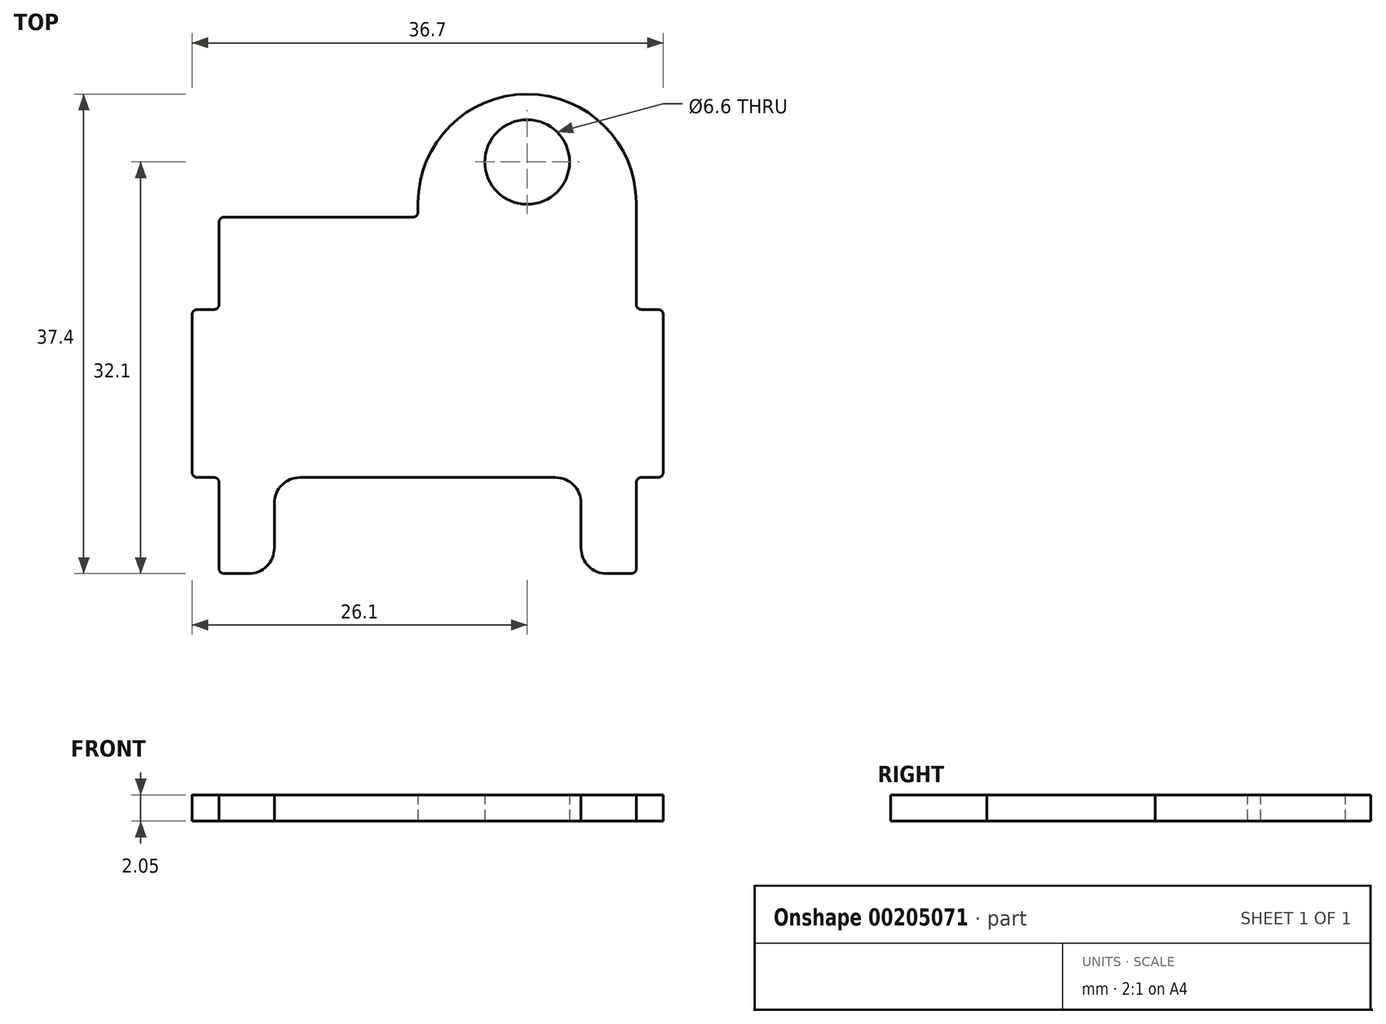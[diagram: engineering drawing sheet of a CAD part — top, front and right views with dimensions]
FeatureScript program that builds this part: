
annotation { "Feature Type Name" : "Feature", "Feature Type Description" : "" }
export const myFeature = defineFeature(function(context is Context, id is Id, definition is map)
    precondition{}
    {
        {
            var Q0;
            Q0=qCreatedBy(makeId("Top.planeOp"),FACE);
            var sketch = newSketch(context, id + "F0", { "sketchPlane" : qUnion([Q0])});
            skLineSegment(sketch, "E0", {"start": v(0, 0) * mm, "end": v(0, -6.8) * mm});
            skLineSegment(sketch, "E1", {"start": v(0.4, -7.2) * mm, "end": v(1.7, -7.2) * mm});
            skLineSegment(sketch, "E2", {"start": v(2.1, -7.6) * mm, "end": v(2.1, -19.9) * mm});
            skLineSegment(sketch, "E3", {"start": v(1.7, -20.3) * mm, "end": v(0.4, -20.3) * mm});
            skLineSegment(sketch, "E4", {"start": v(0, -20.7) * mm, "end": v(0, -27.4) * mm});
            skLineSegment(sketch, "E5", {"start": v(-0.4, -27.8) * mm, "end": v(-2.3, -27.8) * mm});
            skLineSegment(sketch, "E6", {"start": v(-4.3, -25.8) * mm, "end": v(-4.3, -22.3) * mm});
            skLineSegment(sketch, "E7", {"start": v(-6.3, -20.3) * mm, "end": v(-26.2, -20.3) * mm});
            skLineSegment(sketch, "E8", {"start": v(-28.2, -22.3) * mm, "end": v(-28.2, -25.8) * mm});
            skLineSegment(sketch, "E9", {"start": v(-30.2, -27.8) * mm, "end": v(-32.1, -27.8) * mm});
            skLineSegment(sketch, "E10", {"start": v(-32.5, -27.4) * mm, "end": v(-32.5, -20.7) * mm});
            skLineSegment(sketch, "E11", {"start": v(-32.9, -20.3) * mm, "end": v(-34.2, -20.3) * mm});
            skLineSegment(sketch, "E12", {"start": v(-34.6, -19.9) * mm, "end": v(-34.6, -7.6) * mm});
            skLineSegment(sketch, "E13", {"start": v(-34.2, -7.2) * mm, "end": v(-32.9, -7.2) * mm});
            skLineSegment(sketch, "E14", {"start": v(-32.5, -6.8) * mm, "end": v(-32.5, -0.4) * mm});
            skLineSegment(sketch, "E15", {"start": v(-32.1, 0) * mm, "end": v(-17.4, 0) * mm});
            skLineSegment(sketch, "E16", {"start": v(-17, 0.4) * mm, "end": v(-17, 1.1) * mm});
            skLineSegment(sketch, "E17", {"start": v(-8.5, 9.6) * mm, "end": v(-8.5, 9.6) * mm});
            skLineSegment(sketch, "E18", {"start": v(0, 1.1) * mm, "end": v(0, 0) * mm});
            skCircle(sketch, "E19", {"center": v(-8.5, 4.3) * mm, "radius": 3.3 * mm});
            skPoint(sketch, "E20.visualSharp", {"position": v(0, -7.2) * mm});
            skArc(sketch, "E20.filletArc", {"start": v(0, -6.8) * mm, "mid": v(0.12, -7.08) * mm, "end": v(0.4, -7.2) * mm});
            skPoint(sketch, "E21.visualSharp", {"position": v(2.1, -7.2) * mm});
            skArc(sketch, "E21.filletArc", {"start": v(2.1, -7.6) * mm, "mid": v(1.98, -7.32) * mm, "end": v(1.7, -7.2) * mm});
            skPoint(sketch, "E22.visualSharp", {"position": v(2.1, -20.3) * mm});
            skArc(sketch, "E22.filletArc", {"start": v(1.7, -20.3) * mm, "mid": v(1.98, -20.18) * mm, "end": v(2.1, -19.9) * mm});
            skPoint(sketch, "E23.visualSharp", {"position": v(0, -27.8) * mm});
            skArc(sketch, "E23.filletArc", {"start": v(-0.4, -27.8) * mm, "mid": v(-0.12, -27.68) * mm, "end": v(0, -27.4) * mm});
            skPoint(sketch, "E24.visualSharp", {"position": v(0, -20.3) * mm});
            skArc(sketch, "E24.filletArc", {"start": v(0.4, -20.3) * mm, "mid": v(0.12, -20.42) * mm, "end": v(0, -20.7) * mm});
            skPoint(sketch, "E25.visualSharp", {"position": v(-32.5, -27.8) * mm});
            skArc(sketch, "E25.filletArc", {"start": v(-32.5, -27.4) * mm, "mid": v(-32.38, -27.68) * mm, "end": v(-32.1, -27.8) * mm});
            skPoint(sketch, "E26.visualSharp", {"position": v(-32.5, -20.3) * mm});
            skArc(sketch, "E26.filletArc", {"start": v(-32.5, -20.7) * mm, "mid": v(-32.62, -20.42) * mm, "end": v(-32.9, -20.3) * mm});
            skPoint(sketch, "E27.visualSharp", {"position": v(-34.6, -7.2) * mm});
            skArc(sketch, "E27.filletArc", {"start": v(-34.2, -7.2) * mm, "mid": v(-34.48, -7.32) * mm, "end": v(-34.6, -7.6) * mm});
            skPoint(sketch, "E28.visualSharp", {"position": v(-34.6, -20.3) * mm});
            skArc(sketch, "E28.filletArc", {"start": v(-34.6, -19.9) * mm, "mid": v(-34.48, -20.18) * mm, "end": v(-34.2, -20.3) * mm});
            skPoint(sketch, "E29.visualSharp", {"position": v(-32.5, -7.2) * mm});
            skArc(sketch, "E29.filletArc", {"start": v(-32.9, -7.2) * mm, "mid": v(-32.62, -7.08) * mm, "end": v(-32.5, -6.8) * mm});
            skPoint(sketch, "E30.visualSharp", {"position": v(-32.5, 0) * mm});
            skArc(sketch, "E30.filletArc", {"start": v(-32.1, 0) * mm, "mid": v(-32.38, -0.12) * mm, "end": v(-32.5, -0.4) * mm});
            skPoint(sketch, "E31.visualSharp", {"position": v(-17, 0) * mm});
            skArc(sketch, "E31.filletArc", {"start": v(-17.4, 0) * mm, "mid": v(-17.12, 0.12) * mm, "end": v(-17, 0.4) * mm});
            skPoint(sketch, "E32.visualSharp", {"position": v(-4.3, -20.3) * mm});
            skArc(sketch, "E32.filletArc", {"start": v(-4.3, -22.3) * mm, "mid": v(-4.89, -20.89) * mm, "end": v(-6.3, -20.3) * mm});
            skPoint(sketch, "E33.visualSharp", {"position": v(-28.2, -20.3) * mm});
            skArc(sketch, "E33.filletArc", {"start": v(-26.2, -20.3) * mm, "mid": v(-27.61, -20.89) * mm, "end": v(-28.2, -22.3) * mm});
            skPoint(sketch, "E34.visualSharp", {"position": v(-28.2, -27.8) * mm});
            skArc(sketch, "E34.filletArc", {"start": v(-30.2, -27.8) * mm, "mid": v(-28.79, -27.21) * mm, "end": v(-28.2, -25.8) * mm});
            skPoint(sketch, "E35.visualSharp", {"position": v(-4.3, -27.8) * mm});
            skArc(sketch, "E35.filletArc", {"start": v(-4.3, -25.8) * mm, "mid": v(-3.71, -27.21) * mm, "end": v(-2.3, -27.8) * mm});
            skPoint(sketch, "E36.visualSharp", {"position": v(0, 9.6) * mm});
            skArc(sketch, "E36.filletArc", {"start": v(0, 1.1) * mm, "mid": v(-2.49, 7.11) * mm, "end": v(-8.5, 9.6) * mm});
            skPoint(sketch, "E37.visualSharp", {"position": v(-17, 9.6) * mm});
            skArc(sketch, "E37.filletArc", {"start": v(-8.5, 9.6) * mm, "mid": v(-14.51, 7.11) * mm, "end": v(-17, 1.1) * mm});
            skSolve(sketch);
        }
        {
            var Q0;
            Q0 = qSketchRegion(id + "F0", true);
            extrude(context, id + "F1", {"entities" : qUnion([Q0]), "depth" : 2.05 * mm});
        }
    });
